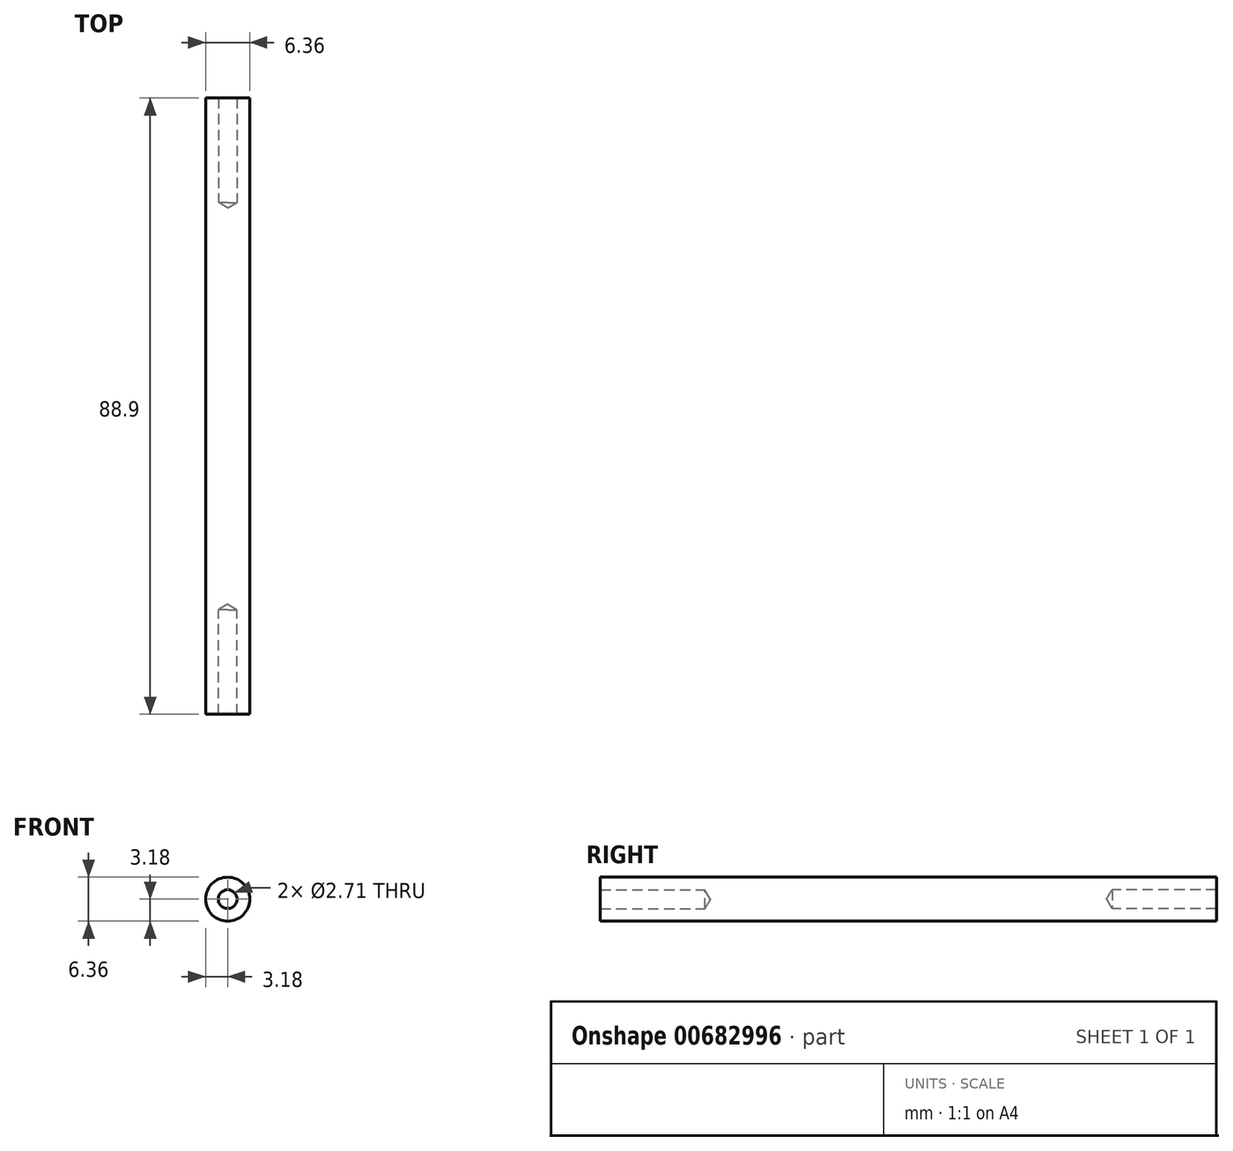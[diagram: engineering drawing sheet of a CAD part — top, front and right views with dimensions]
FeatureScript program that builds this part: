
annotation { "Feature Type Name" : "Feature", "Feature Type Description" : "" }
export const myFeature = defineFeature(function(context is Context, id is Id, definition is map)
    precondition{}
    {
        {
            var Q0;
            Q0=qCreatedBy(makeId("Front.planeOp"),FACE);
            var sketch = newSketch(context, id + "F0", { "sketchPlane" : qUnion([Q0])});
            skCircle(sketch, "E0", {"center": v(0, 0) * mm, "radius": 3.18 * mm});
            skSolve(sketch);
        }
        {
            var Q0;
            Q0=makeQuery(id+"F0.imprint","IMPRINT",FACE,{"disambiguationData":[TD([[makeQuery(id+"F0.imprint","IMPRINT",EDGE,{"derivedFrom":sQuery(id+"F0.wireOp",EDGE,"E0")}),1.0]])]});
            extrude(context, id + "F1", {"entities" : qUnion([Q0]), "depth" : 88.9 * mm, "offsetDistance" : 25.4 * mm});
        }
        {
            var Q0;
            Q0=makeQuery(id+"F1.opExtrude","CAP_FACE",FACE,{"disambiguationData":[OSD([sQuery(id+"F0.wireOp",EDGE,"E0")])],"isStart":false});
            var sketch = newSketch(context, id + "F2", { "sketchPlane" : qUnion([Q0])});
            skPoint(sketch, "E1", {"position": v(0, 0) * mm});
            skSolve(sketch);
        }
        {
            var Q0;
            Q0=makeQuery(id+"F1.opExtrude","CAP_FACE",FACE,{"disambiguationData":[OSD([sQuery(id+"F0.wireOp",EDGE,"E0")])],"isStart":true});
            var sketch = newSketch(context, id + "F3", { "sketchPlane" : qUnion([Q0])});
            skPoint(sketch, "E2", {"position": v(0, 0) * mm});
            skSolve(sketch);
        }
        {
            var Q0;
            Q0=sQuery(id+"F3.wireOp",VERTEX,"E2");
            var Q1;
            Q1=sQuery(id+"F2.wireOp",VERTEX,"E1");
            var Q2;
            Q2=makeQuery(id+"F1.opExtrude","SWEPT_BODY",BODY,{"disambiguationData":[OSD([sQuery(id+"F0.wireOp",EDGE,"E0")])]});
            hole(context, id + "F4", {"style" : HoleStyle.SIMPLE, "endStyle" : HoleEndStyle.BLIND, "standardTappedOrClearance" : lookupTablePath({ "standard" : "ANSI", "engagement" : "75%", "pitch" : "32 tpi", "size" : "#6", "type" : "Tapped" }), "standardBlindInLast" : lookupTablePath({ "standard" : "ANSI", "engagement" : "75%", "pitch" : "32 tpi", "size" : "#6", "type" : "Tapped" }), "holeDiameter" : 2.7 * mm, "majorDiameter" : 3.5 * mm, "showTappedDepth" : true, "holeDepth" : 15.08 * mm, "tappedDepth" : 12.7 * mm, "tapClearance" : 3, "locations" : qUnion([Q0, Q1]), "scope" : qUnion([Q2]), "startStyle" : HoleStartStyle.SKETCH});
        }
    });
